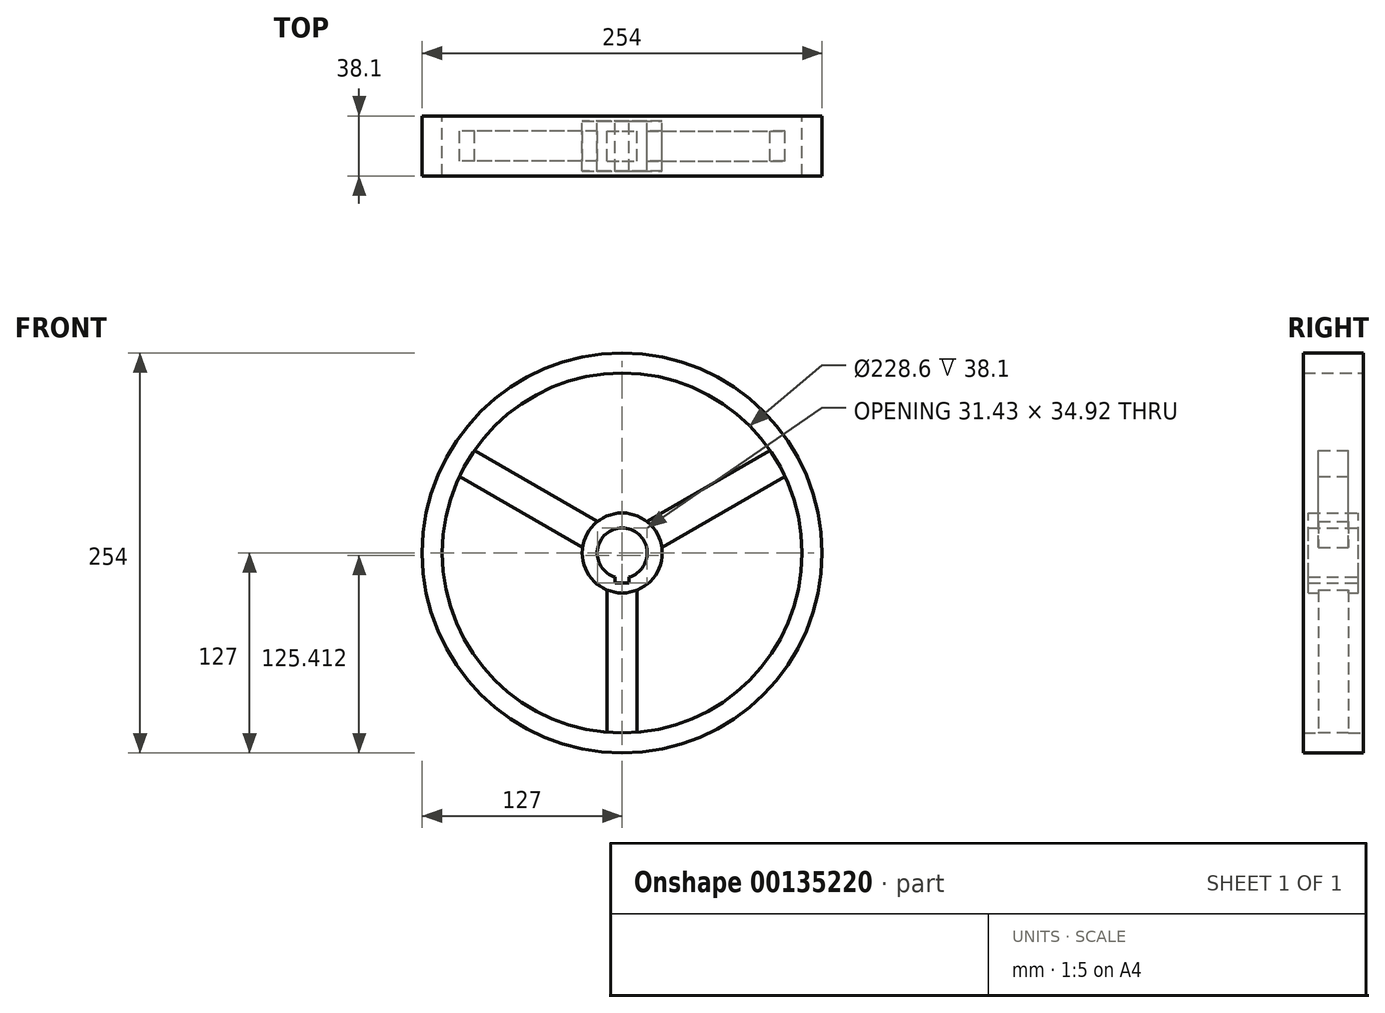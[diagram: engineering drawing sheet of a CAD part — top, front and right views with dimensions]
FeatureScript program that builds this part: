
annotation { "Feature Type Name" : "Feature", "Feature Type Description" : "" }
export const myFeature = defineFeature(function(context is Context, id is Id, definition is map)
    precondition{}
    {
        {
            var Q0;
            Q0=qCreatedBy(makeId("Front.planeOp"),FACE);
            var sketch = newSketch(context, id + "F0", { "sketchPlane" : qUnion([Q0])});
            skCircle(sketch, "E0", {"center": v(0, 0) * mm, "radius": 127 * mm});
            skCircle(sketch, "E1", {"center": v(0, 0) * mm, "radius": 114.3 * mm});
            skCircle(sketch, "E2", {"center": v(0, 0) * mm, "radius": 25.4 * mm});
            skArc(sketch, "E3", {"start": v(4.45, -15.24) * mm, "mid": v(0, 15.88) * mm, "end": v(-4.45, -15.24) * mm});
            skLineSegment(sketch, "E4", {"start": v(0, -19.05) * mm, "end": v(4.45, -19.05) * mm});
            skLineSegment(sketch, "E5.MirrorCS", {"start": v(0, -19.05) * mm, "end": v(-4.45, -19.05) * mm});
            skLineSegment(sketch, "E6", {"start": v(-4.45, -19.05) * mm, "end": v(-4.45, -15.24) * mm});
            skLineSegment(sketch, "E7", {"start": v(4.45, -19.05) * mm, "end": v(4.45, -15.24) * mm});
            skLineSegment(sketch, "E8", {"start": v(-9.53, -23.55) * mm, "end": v(-9.53, -113.9) * mm});
            skLineSegment(sketch, "E9.MirrorCS", {"start": v(9.53, -23.55) * mm, "end": v(9.53, -113.9) * mm});
            skLineSegment(sketch, "E10.1.0", {"start": v(-15.63, 20.02) * mm, "end": v(-93.88, 65.2) * mm});
            skLineSegment(sketch, "E10.1.1", {"start": v(-25.15, 3.52) * mm, "end": v(-103.4, 48.7) * mm});
            skLineSegment(sketch, "E10.2.0", {"start": v(25.15, 3.52) * mm, "end": v(103.4, 48.7) * mm});
            skLineSegment(sketch, "E10.2.1", {"start": v(15.63, 20.02) * mm, "end": v(93.88, 65.2) * mm});
            skLineSegment(sketch, "E10.anchor1", {"start": v(0, 0) * mm, "end": v(-9.53, -113.9) * mm, "construction": true});
            skLineSegment(sketch, "E10.anchor2", {"start": v(0, 0) * mm, "end": v(103.4, 48.7) * mm, "construction": true});
            skSolve(sketch);
        }
        {
            var Q0;
            Q0=makeQuery(id+"F0.imprint","IMPRINT",FACE,{"disambiguationData":[TD([[makeQuery(id+"F0.imprint","IMPRINT",EDGE,{"derivedFrom":sQuery(id+"F0.wireOp",EDGE,"E3")}),-1.0]])]});
            extrude(context, id + "F1", {"entities" : qUnion([Q0]), "endBound" : BoundingType.SYMMETRIC, "depth" : 31.75 * mm});
        }
        {
            var Q0;
            {var subQ0=sQuery(id+"F0.wireOp",EDGE,"E10.1.0");Q0=makeQuery(id+"F0.imprint","IMPRINT",FACE,{"disambiguationData":[TD([[makeQuery(id+"F0.imprint","IMPRINT",EDGE,{"derivedFrom":subQ0}),1.0]])]});}
            var Q1;
            {var subQ0=sQuery(id+"F0.wireOp",EDGE,"E10.2.0");Q1=makeQuery(id+"F0.imprint","IMPRINT",FACE,{"disambiguationData":[TD([[makeQuery(id+"F0.imprint","IMPRINT",EDGE,{"derivedFrom":subQ0}),1.0]])]});}
            var Q2;
            {var subQ0=sQuery(id+"F0.wireOp",EDGE,"E8");Q2=makeQuery(id+"F0.imprint","IMPRINT",FACE,{"disambiguationData":[TD([[makeQuery(id+"F0.imprint","IMPRINT",EDGE,{"derivedFrom":subQ0}),1.0]])]});}
            extrude(context, id + "F2", {"entities" : qUnion([Q0, Q1, Q2]), "operationType" : NewBodyOperationType.ADD, "endBound" : BoundingType.SYMMETRIC, "depth" : 19.05 * mm});
        }
        {
            var Q0;
            Q0=makeQuery(id+"F0.imprint","IMPRINT",FACE,{"disambiguationData":[TD([[makeQuery(id+"F0.imprint","IMPRINT",EDGE,{"derivedFrom":sQuery(id+"F0.wireOp",EDGE,"E0")}),1.0]])]});
            extrude(context, id + "F3", {"entities" : qUnion([Q0]), "operationType" : NewBodyOperationType.ADD, "endBound" : BoundingType.SYMMETRIC, "depth" : 38.1 * mm});
        }
    });
